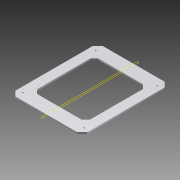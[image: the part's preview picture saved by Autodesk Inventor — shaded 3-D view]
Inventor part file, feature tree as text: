
AUTODESK INVENTOR PART (.ipt)
format: ipt  version: 2015 (Build 190159000, 159)  size: 165,376 bytes
history: native  units: mm
features: extrude x3, fillet x1, chamfer x1, hole x1, projected_geometry x1
ambient origin geometry x8: Origin, YZ Plane, XZ Plane, XY Plane, X Axis, Y Axis, Z Axis, Center Point
bodies: Solid1 (feature_tree)
feature tree (7):
  extrude  "Extrusión1"  Depth=359.0mm
  fillet  "Empalme1"  Radius=436.5mm
  chamfer  "Chaflán1"  Distance=65.0mm
  hole  "Agujero1"  [1 undecoded]
  extrude  "Extrusión4"  TaperAngle=45.0deg  [1 undecoded]
  extrude  "Extrusión3"  Depth=20.0mm
  projected_geometry  "Contorno proyectado1"
note: 2 required parameter values undecoded (feature->parameter linkage not recoverable at this tier; creation-order binding heuristic only, values carry confidence <= 0.55)
